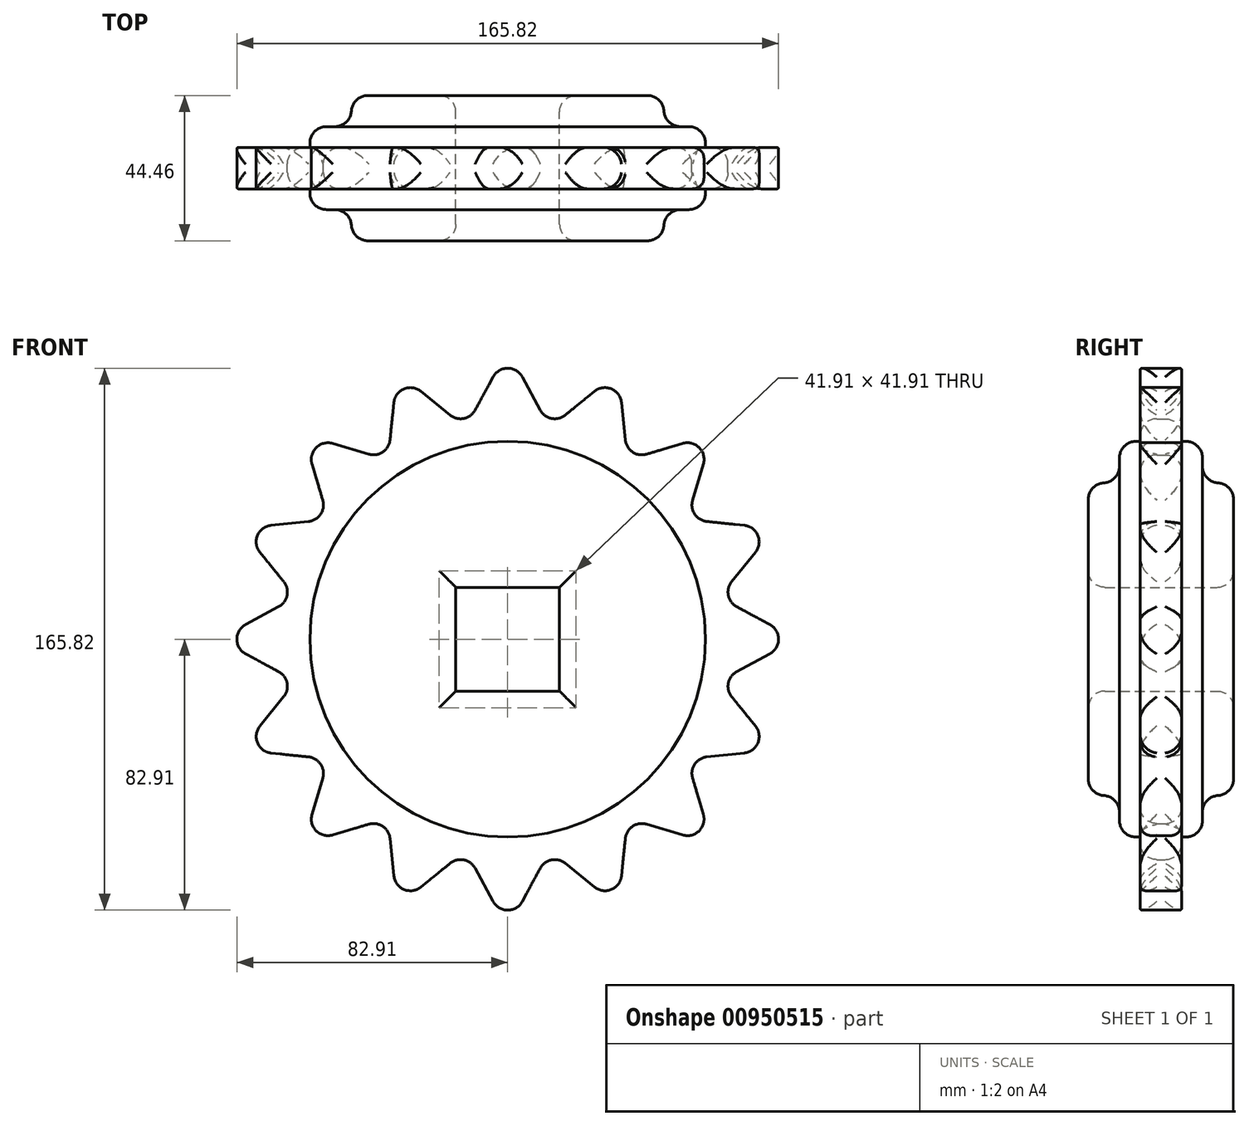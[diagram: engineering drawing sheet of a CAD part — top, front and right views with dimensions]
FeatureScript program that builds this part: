
annotation { "Feature Type Name" : "Feature", "Feature Type Description" : "" }
export const myFeature = defineFeature(function(context is Context, id is Id, definition is map)
    precondition{}
    {
        {
            var Q0;
            Q0=qCreatedBy(makeId("Front.planeOp"),FACE);
            var sketch = newSketch(context, id + "F0", { "sketchPlane" : qUnion([Q0])});
            skCircle(sketch, "E0", {"center": v(0, 0) * mm, "radius": 47.85 * mm});
            skLineSegment(sketch, "E1.bottom", {"start": v(-15.87, 15.88) * mm, "end": v(15.88, 15.88) * mm});
            skLineSegment(sketch, "E1.top", {"start": v(-15.88, -15.88) * mm, "end": v(15.87, -15.88) * mm});
            skLineSegment(sketch, "E1.left", {"start": v(-15.87, 15.88) * mm, "end": v(-15.88, -15.88) * mm});
            skLineSegment(sketch, "E1.right", {"start": v(15.88, 15.88) * mm, "end": v(15.87, -15.88) * mm});
            skCircle(sketch, "E2", {"center": v(0, 0) * mm, "radius": 60.55 * mm});
            skLineSegment(sketch, "E3", {"start": v(-16.33, 58.3) * mm, "end": v(0, 88.51) * mm});
            skLineSegment(sketch, "E4", {"start": v(16.33, 58.3) * mm, "end": v(0, 88.51) * mm});
            skLineSegment(sketch, "E5.1.0", {"start": v(-7.23, 60.12) * mm, "end": v(-33.87, 81.77) * mm});
            skLineSegment(sketch, "E5.2.0", {"start": v(-29.68, 52.78) * mm, "end": v(-62.59, 62.59) * mm});
            skLineSegment(sketch, "E5.3.0", {"start": v(-47.62, 37.4) * mm, "end": v(-81.77, 33.87) * mm});
            skLineSegment(sketch, "E5.4.0", {"start": v(-58.3, 16.33) * mm, "end": v(-88.51, 0) * mm});
            skLineSegment(sketch, "E5.5.0", {"start": v(-60.12, -7.23) * mm, "end": v(-81.77, -33.87) * mm});
            skLineSegment(sketch, "E5.6.0", {"start": v(-52.78, -29.68) * mm, "end": v(-62.59, -62.59) * mm});
            skLineSegment(sketch, "E5.7.0", {"start": v(-37.4, -47.62) * mm, "end": v(-33.87, -81.77) * mm});
            skLineSegment(sketch, "E5.8.0", {"start": v(-16.33, -58.3) * mm, "end": v(0, -88.51) * mm});
            skLineSegment(sketch, "E5.9.0", {"start": v(7.23, -60.12) * mm, "end": v(33.87, -81.77) * mm});
            skLineSegment(sketch, "E5.10.0", {"start": v(29.68, -52.78) * mm, "end": v(62.59, -62.59) * mm});
            skLineSegment(sketch, "E5.11.0", {"start": v(47.62, -37.4) * mm, "end": v(81.77, -33.87) * mm});
            skLineSegment(sketch, "E5.12.0", {"start": v(58.3, -16.33) * mm, "end": v(88.51, 0) * mm});
            skLineSegment(sketch, "E5.13.0", {"start": v(60.12, 7.23) * mm, "end": v(81.77, 33.87) * mm});
            skLineSegment(sketch, "E5.14.0", {"start": v(52.78, 29.68) * mm, "end": v(62.59, 62.59) * mm});
            skLineSegment(sketch, "E5.15.0", {"start": v(37.4, 47.62) * mm, "end": v(33.87, 81.77) * mm});
            skLineSegment(sketch, "E6.1.0", {"start": v(-37.4, 47.62) * mm, "end": v(-33.87, 81.77) * mm});
            skLineSegment(sketch, "E6.2.0", {"start": v(-52.78, 29.68) * mm, "end": v(-62.59, 62.59) * mm});
            skLineSegment(sketch, "E6.3.0", {"start": v(-60.12, 7.23) * mm, "end": v(-81.77, 33.87) * mm});
            skLineSegment(sketch, "E6.4.0", {"start": v(-58.3, -16.33) * mm, "end": v(-88.51, 0) * mm});
            skLineSegment(sketch, "E6.5.0", {"start": v(-47.62, -37.4) * mm, "end": v(-81.77, -33.87) * mm});
            skLineSegment(sketch, "E6.6.0", {"start": v(-29.68, -52.78) * mm, "end": v(-62.59, -62.59) * mm});
            skLineSegment(sketch, "E6.7.0", {"start": v(-7.23, -60.12) * mm, "end": v(-33.87, -81.77) * mm});
            skLineSegment(sketch, "E6.8.0", {"start": v(16.33, -58.3) * mm, "end": v(0, -88.51) * mm});
            skLineSegment(sketch, "E6.9.0", {"start": v(37.4, -47.62) * mm, "end": v(33.87, -81.77) * mm});
            skLineSegment(sketch, "E6.10.0", {"start": v(52.78, -29.68) * mm, "end": v(62.59, -62.59) * mm});
            skLineSegment(sketch, "E6.11.0", {"start": v(60.12, -7.23) * mm, "end": v(81.77, -33.87) * mm});
            skLineSegment(sketch, "E6.12.0", {"start": v(58.3, 16.33) * mm, "end": v(88.51, 0) * mm});
            skLineSegment(sketch, "E6.13.0", {"start": v(47.62, 37.4) * mm, "end": v(81.77, 33.87) * mm});
            skLineSegment(sketch, "E6.14.0", {"start": v(29.68, 52.78) * mm, "end": v(62.59, 62.59) * mm});
            skLineSegment(sketch, "E6.15.0", {"start": v(7.23, 60.12) * mm, "end": v(33.87, 81.77) * mm});
            skSolve(sketch);
        }
        {
            var Q0;
            {var subQ1=sQuery(id+"F0.wireOp",EDGE,"E2");var subQ7=sQuery(id+"F0.wireOp",EDGE,"E3");var subQ9=makeQuery(id+"F0.imprint","INTERSECT",VERTEX,{"derivedFrom":[subQ1,subQ7]});Q0=makeQuery(id+"F0.imprint","IMPRINT",FACE,{"disambiguationData":[TD([[makeQuery(id+"F0.imprint","IMPRINT",EDGE,{"disambiguationData":[TD([[subQ9,-1.0]])],"derivedFrom":subQ1}),-1.0]])]});}
            var Q1;
            {var subQ0=sQuery(id+"F0.wireOp",EDGE,"E5.3.0");var subQ1=sQuery(id+"F0.wireOp",EDGE,"E2");var subQ2=makeQuery(id+"F0.imprint","INTERSECT",VERTEX,{"derivedFrom":[subQ1,subQ0]});Q1=makeQuery(id+"F0.imprint","IMPRINT",FACE,{"disambiguationData":[TD([[makeQuery(id+"F0.imprint","IMPRINT",EDGE,{"disambiguationData":[TD([[subQ2,1.0]])],"derivedFrom":subQ1}),-1.0]])]});}
            var Q2;
            {var subQ0=sQuery(id+"F0.wireOp",EDGE,"E5.2.0");var subQ1=sQuery(id+"F0.wireOp",EDGE,"E2");var subQ2=makeQuery(id+"F0.imprint","INTERSECT",VERTEX,{"derivedFrom":[subQ1,subQ0]});Q2=makeQuery(id+"F0.imprint","IMPRINT",FACE,{"disambiguationData":[TD([[makeQuery(id+"F0.imprint","IMPRINT",EDGE,{"disambiguationData":[TD([[subQ2,-1.0]])],"derivedFrom":subQ1}),-1.0]])]});}
            var Q3;
            {var subQ0=sQuery(id+"F0.wireOp",EDGE,"E5.4.0");var subQ1=sQuery(id+"F0.wireOp",EDGE,"E2");var subQ2=makeQuery(id+"F0.imprint","INTERSECT",VERTEX,{"derivedFrom":[subQ1,subQ0]});Q3=makeQuery(id+"F0.imprint","IMPRINT",FACE,{"disambiguationData":[TD([[makeQuery(id+"F0.imprint","IMPRINT",EDGE,{"disambiguationData":[TD([[subQ2,1.0]])],"derivedFrom":subQ1}),-1.0]])]});}
            var Q4;
            {var subQ0=sQuery(id+"F0.wireOp",EDGE,"E5.5.0");var subQ1=sQuery(id+"F0.wireOp",EDGE,"E2");var subQ2=makeQuery(id+"F0.imprint","INTERSECT",VERTEX,{"derivedFrom":[subQ1,subQ0]});Q4=makeQuery(id+"F0.imprint","IMPRINT",FACE,{"disambiguationData":[TD([[makeQuery(id+"F0.imprint","IMPRINT",EDGE,{"disambiguationData":[TD([[subQ2,1.0]])],"derivedFrom":subQ1}),-1.0]])]});}
            var Q5;
            {var subQ0=sQuery(id+"F0.wireOp",EDGE,"E5.6.0");var subQ1=sQuery(id+"F0.wireOp",EDGE,"E2");var subQ2=makeQuery(id+"F0.imprint","INTERSECT",VERTEX,{"derivedFrom":[subQ1,subQ0]});Q5=makeQuery(id+"F0.imprint","IMPRINT",FACE,{"disambiguationData":[TD([[makeQuery(id+"F0.imprint","IMPRINT",EDGE,{"disambiguationData":[TD([[subQ2,1.0]])],"derivedFrom":subQ1}),-1.0]])]});}
            var Q6;
            {var subQ0=sQuery(id+"F0.wireOp",EDGE,"E5.7.0");var subQ1=sQuery(id+"F0.wireOp",EDGE,"E2");var subQ2=makeQuery(id+"F0.imprint","INTERSECT",VERTEX,{"derivedFrom":[subQ1,subQ0]});Q6=makeQuery(id+"F0.imprint","IMPRINT",FACE,{"disambiguationData":[TD([[makeQuery(id+"F0.imprint","IMPRINT",EDGE,{"disambiguationData":[TD([[subQ2,1.0]])],"derivedFrom":subQ1}),-1.0]])]});}
            var Q7;
            {var subQ0=sQuery(id+"F0.wireOp",EDGE,"E5.8.0");var subQ1=sQuery(id+"F0.wireOp",EDGE,"E2");var subQ2=makeQuery(id+"F0.imprint","INTERSECT",VERTEX,{"derivedFrom":[subQ1,subQ0]});Q7=makeQuery(id+"F0.imprint","IMPRINT",FACE,{"disambiguationData":[TD([[makeQuery(id+"F0.imprint","IMPRINT",EDGE,{"disambiguationData":[TD([[subQ2,1.0]])],"derivedFrom":subQ1}),-1.0]])]});}
            var Q8;
            {var subQ0=sQuery(id+"F0.wireOp",EDGE,"E5.9.0");var subQ1=sQuery(id+"F0.wireOp",EDGE,"E2");var subQ2=makeQuery(id+"F0.imprint","INTERSECT",VERTEX,{"derivedFrom":[subQ1,subQ0]});Q8=makeQuery(id+"F0.imprint","IMPRINT",FACE,{"disambiguationData":[TD([[makeQuery(id+"F0.imprint","IMPRINT",EDGE,{"disambiguationData":[TD([[subQ2,1.0]])],"derivedFrom":subQ1}),-1.0]])]});}
            var Q9;
            {var subQ0=sQuery(id+"F0.wireOp",EDGE,"E5.10.0");var subQ1=sQuery(id+"F0.wireOp",EDGE,"E2");var subQ2=makeQuery(id+"F0.imprint","INTERSECT",VERTEX,{"derivedFrom":[subQ1,subQ0]});Q9=makeQuery(id+"F0.imprint","IMPRINT",FACE,{"disambiguationData":[TD([[makeQuery(id+"F0.imprint","IMPRINT",EDGE,{"disambiguationData":[TD([[subQ2,1.0]])],"derivedFrom":subQ1}),-1.0]])]});}
            var Q10;
            {var subQ0=sQuery(id+"F0.wireOp",EDGE,"E5.11.0");var subQ1=sQuery(id+"F0.wireOp",EDGE,"E2");var subQ2=makeQuery(id+"F0.imprint","INTERSECT",VERTEX,{"derivedFrom":[subQ1,subQ0]});Q10=makeQuery(id+"F0.imprint","IMPRINT",FACE,{"disambiguationData":[TD([[makeQuery(id+"F0.imprint","IMPRINT",EDGE,{"disambiguationData":[TD([[subQ2,1.0]])],"derivedFrom":subQ1}),-1.0]])]});}
            var Q11;
            {var subQ0=sQuery(id+"F0.wireOp",EDGE,"E5.12.0");var subQ1=sQuery(id+"F0.wireOp",EDGE,"E2");var subQ2=makeQuery(id+"F0.imprint","INTERSECT",VERTEX,{"derivedFrom":[subQ1,subQ0]});Q11=makeQuery(id+"F0.imprint","IMPRINT",FACE,{"disambiguationData":[TD([[makeQuery(id+"F0.imprint","IMPRINT",EDGE,{"disambiguationData":[TD([[subQ2,1.0]])],"derivedFrom":subQ1}),-1.0]])]});}
            var Q12;
            {var subQ0=sQuery(id+"F0.wireOp",EDGE,"E5.13.0");var subQ1=sQuery(id+"F0.wireOp",EDGE,"E2");var subQ2=makeQuery(id+"F0.imprint","INTERSECT",VERTEX,{"derivedFrom":[subQ1,subQ0]});Q12=makeQuery(id+"F0.imprint","IMPRINT",FACE,{"disambiguationData":[TD([[makeQuery(id+"F0.imprint","IMPRINT",EDGE,{"disambiguationData":[TD([[subQ2,1.0]])],"derivedFrom":subQ1}),-1.0]])]});}
            var Q13;
            {var subQ1=sQuery(id+"F0.wireOp",EDGE,"E2");var subQ5=sQuery(id+"F0.wireOp",EDGE,"E5.14.0");var subQ6=makeQuery(id+"F0.imprint","INTERSECT",VERTEX,{"derivedFrom":[subQ1,subQ5]});Q13=makeQuery(id+"F0.imprint","IMPRINT",FACE,{"disambiguationData":[TD([[makeQuery(id+"F0.imprint","IMPRINT",EDGE,{"disambiguationData":[TD([[subQ6,1.0]])],"derivedFrom":subQ1}),-1.0]])]});}
            var Q14;
            {var subQ1=sQuery(id+"F0.wireOp",EDGE,"E2");var subQ5=sQuery(id+"F0.wireOp",EDGE,"E5.15.0");var subQ6=makeQuery(id+"F0.imprint","INTERSECT",VERTEX,{"derivedFrom":[subQ1,subQ5]});Q14=makeQuery(id+"F0.imprint","IMPRINT",FACE,{"disambiguationData":[TD([[makeQuery(id+"F0.imprint","IMPRINT",EDGE,{"disambiguationData":[TD([[subQ6,1.0]])],"derivedFrom":subQ1}),-1.0]])]});}
            var Q15;
            {var subQ1=sQuery(id+"F0.wireOp",EDGE,"E2");var subQ5=sQuery(id+"F0.wireOp",EDGE,"E4");var subQ6=makeQuery(id+"F0.imprint","INTERSECT",VERTEX,{"derivedFrom":[subQ1,subQ5]});Q15=makeQuery(id+"F0.imprint","IMPRINT",FACE,{"disambiguationData":[TD([[makeQuery(id+"F0.imprint","IMPRINT",EDGE,{"disambiguationData":[TD([[subQ6,1.0]])],"derivedFrom":subQ1}),-1.0]])]});}
            var Q16;
            {var subQ0=sQuery(id+"F0.wireOp",EDGE,"E5.1.0");var subQ1=sQuery(id+"F0.wireOp",EDGE,"E2");var subQ2=makeQuery(id+"F0.imprint","INTERSECT",VERTEX,{"derivedFrom":[subQ1,subQ0]});Q16=makeQuery(id+"F0.imprint","IMPRINT",FACE,{"disambiguationData":[TD([[makeQuery(id+"F0.imprint","IMPRINT",EDGE,{"disambiguationData":[TD([[subQ2,1.0]])],"derivedFrom":subQ1}),-1.0]])]});}
            var Q17;
            {var subQ0=sQuery(id+"F0.wireOp",EDGE,"E3");var subQ1=sQuery(id+"F0.wireOp",EDGE,"E2");var subQ2=makeQuery(id+"F0.imprint","INTERSECT",VERTEX,{"derivedFrom":[subQ1,subQ0]});Q17=makeQuery(id+"F0.imprint","IMPRINT",FACE,{"disambiguationData":[TD([[makeQuery(id+"F0.imprint","IMPRINT",EDGE,{"disambiguationData":[TD([[subQ2,1.0]])],"derivedFrom":subQ1}),-1.0]])]});}
            var Q18;
            {var subQ0=sQuery(id+"F0.wireOp",EDGE,"E4");var subQ1=sQuery(id+"F0.wireOp",EDGE,"E2");var subQ2=makeQuery(id+"F0.imprint","INTERSECT",VERTEX,{"derivedFrom":[subQ1,subQ0]});Q18=makeQuery(id+"F0.imprint","IMPRINT",FACE,{"disambiguationData":[TD([[makeQuery(id+"F0.imprint","IMPRINT",EDGE,{"disambiguationData":[TD([[subQ2,-1.0]])],"derivedFrom":subQ1}),-1.0]])]});}
            var Q19;
            {var subQ0=sQuery(id+"F0.wireOp",EDGE,"E5.15.0");var subQ1=sQuery(id+"F0.wireOp",EDGE,"E2");var subQ2=makeQuery(id+"F0.imprint","INTERSECT",VERTEX,{"derivedFrom":[subQ1,subQ0]});Q19=makeQuery(id+"F0.imprint","IMPRINT",FACE,{"disambiguationData":[TD([[makeQuery(id+"F0.imprint","IMPRINT",EDGE,{"disambiguationData":[TD([[subQ2,-1.0]])],"derivedFrom":subQ1}),-1.0]])]});}
            var Q20;
            {var subQ0=sQuery(id+"F0.wireOp",EDGE,"E5.14.0");var subQ1=sQuery(id+"F0.wireOp",EDGE,"E2");var subQ2=makeQuery(id+"F0.imprint","INTERSECT",VERTEX,{"derivedFrom":[subQ1,subQ0]});Q20=makeQuery(id+"F0.imprint","IMPRINT",FACE,{"disambiguationData":[TD([[makeQuery(id+"F0.imprint","IMPRINT",EDGE,{"disambiguationData":[TD([[subQ2,-1.0]])],"derivedFrom":subQ1}),-1.0]])]});}
            var Q21;
            {var subQ0=sQuery(id+"F0.wireOp",EDGE,"E5.13.0");var subQ1=sQuery(id+"F0.wireOp",EDGE,"E2");var subQ2=makeQuery(id+"F0.imprint","INTERSECT",VERTEX,{"derivedFrom":[subQ1,subQ0]});Q21=makeQuery(id+"F0.imprint","IMPRINT",FACE,{"disambiguationData":[TD([[makeQuery(id+"F0.imprint","IMPRINT",EDGE,{"disambiguationData":[TD([[subQ2,-1.0]])],"derivedFrom":subQ1}),-1.0]])]});}
            var Q22;
            {var subQ0=sQuery(id+"F0.wireOp",EDGE,"E5.3.0");var subQ1=sQuery(id+"F0.wireOp",EDGE,"E2");var subQ2=makeQuery(id+"F0.imprint","INTERSECT",VERTEX,{"derivedFrom":[subQ1,subQ0]});Q22=makeQuery(id+"F0.imprint","IMPRINT",FACE,{"disambiguationData":[TD([[makeQuery(id+"F0.imprint","IMPRINT",EDGE,{"disambiguationData":[TD([[subQ2,-1.0]])],"derivedFrom":subQ1}),-1.0]])]});}
            var Q23;
            {var subQ0=sQuery(id+"F0.wireOp",EDGE,"E5.4.0");var subQ1=sQuery(id+"F0.wireOp",EDGE,"E2");var subQ2=makeQuery(id+"F0.imprint","INTERSECT",VERTEX,{"derivedFrom":[subQ1,subQ0]});Q23=makeQuery(id+"F0.imprint","IMPRINT",FACE,{"disambiguationData":[TD([[makeQuery(id+"F0.imprint","IMPRINT",EDGE,{"disambiguationData":[TD([[subQ2,-1.0]])],"derivedFrom":subQ1}),-1.0]])]});}
            var Q24;
            {var subQ0=sQuery(id+"F0.wireOp",EDGE,"E5.5.0");var subQ1=sQuery(id+"F0.wireOp",EDGE,"E2");var subQ2=makeQuery(id+"F0.imprint","INTERSECT",VERTEX,{"derivedFrom":[subQ1,subQ0]});Q24=makeQuery(id+"F0.imprint","IMPRINT",FACE,{"disambiguationData":[TD([[makeQuery(id+"F0.imprint","IMPRINT",EDGE,{"disambiguationData":[TD([[subQ2,-1.0]])],"derivedFrom":subQ1}),-1.0]])]});}
            var Q25;
            {var subQ0=sQuery(id+"F0.wireOp",EDGE,"E5.6.0");var subQ1=sQuery(id+"F0.wireOp",EDGE,"E2");var subQ2=makeQuery(id+"F0.imprint","INTERSECT",VERTEX,{"derivedFrom":[subQ1,subQ0]});Q25=makeQuery(id+"F0.imprint","IMPRINT",FACE,{"disambiguationData":[TD([[makeQuery(id+"F0.imprint","IMPRINT",EDGE,{"disambiguationData":[TD([[subQ2,-1.0]])],"derivedFrom":subQ1}),-1.0]])]});}
            var Q26;
            {var subQ0=sQuery(id+"F0.wireOp",EDGE,"E5.7.0");var subQ1=sQuery(id+"F0.wireOp",EDGE,"E2");var subQ2=makeQuery(id+"F0.imprint","INTERSECT",VERTEX,{"derivedFrom":[subQ1,subQ0]});Q26=makeQuery(id+"F0.imprint","IMPRINT",FACE,{"disambiguationData":[TD([[makeQuery(id+"F0.imprint","IMPRINT",EDGE,{"disambiguationData":[TD([[subQ2,-1.0]])],"derivedFrom":subQ1}),-1.0]])]});}
            var Q27;
            {var subQ0=sQuery(id+"F0.wireOp",EDGE,"E5.8.0");var subQ1=sQuery(id+"F0.wireOp",EDGE,"E2");var subQ2=makeQuery(id+"F0.imprint","INTERSECT",VERTEX,{"derivedFrom":[subQ1,subQ0]});Q27=makeQuery(id+"F0.imprint","IMPRINT",FACE,{"disambiguationData":[TD([[makeQuery(id+"F0.imprint","IMPRINT",EDGE,{"disambiguationData":[TD([[subQ2,-1.0]])],"derivedFrom":subQ1}),-1.0]])]});}
            var Q28;
            {var subQ0=sQuery(id+"F0.wireOp",EDGE,"E5.9.0");var subQ1=sQuery(id+"F0.wireOp",EDGE,"E2");var subQ2=makeQuery(id+"F0.imprint","INTERSECT",VERTEX,{"derivedFrom":[subQ1,subQ0]});Q28=makeQuery(id+"F0.imprint","IMPRINT",FACE,{"disambiguationData":[TD([[makeQuery(id+"F0.imprint","IMPRINT",EDGE,{"disambiguationData":[TD([[subQ2,-1.0]])],"derivedFrom":subQ1}),-1.0]])]});}
            var Q29;
            {var subQ0=sQuery(id+"F0.wireOp",EDGE,"E5.10.0");var subQ1=sQuery(id+"F0.wireOp",EDGE,"E2");var subQ2=makeQuery(id+"F0.imprint","INTERSECT",VERTEX,{"derivedFrom":[subQ1,subQ0]});Q29=makeQuery(id+"F0.imprint","IMPRINT",FACE,{"disambiguationData":[TD([[makeQuery(id+"F0.imprint","IMPRINT",EDGE,{"disambiguationData":[TD([[subQ2,-1.0]])],"derivedFrom":subQ1}),-1.0]])]});}
            var Q30;
            {var subQ0=sQuery(id+"F0.wireOp",EDGE,"E5.11.0");var subQ1=sQuery(id+"F0.wireOp",EDGE,"E2");var subQ2=makeQuery(id+"F0.imprint","INTERSECT",VERTEX,{"derivedFrom":[subQ1,subQ0]});Q30=makeQuery(id+"F0.imprint","IMPRINT",FACE,{"disambiguationData":[TD([[makeQuery(id+"F0.imprint","IMPRINT",EDGE,{"disambiguationData":[TD([[subQ2,-1.0]])],"derivedFrom":subQ1}),-1.0]])]});}
            var Q31;
            {var subQ0=sQuery(id+"F0.wireOp",EDGE,"E5.12.0");var subQ1=sQuery(id+"F0.wireOp",EDGE,"E2");var subQ2=makeQuery(id+"F0.imprint","INTERSECT",VERTEX,{"derivedFrom":[subQ1,subQ0]});Q31=makeQuery(id+"F0.imprint","IMPRINT",FACE,{"disambiguationData":[TD([[makeQuery(id+"F0.imprint","IMPRINT",EDGE,{"disambiguationData":[TD([[subQ2,-1.0]])],"derivedFrom":subQ1}),-1.0]])]});}
            extrude(context, id + "F1", {"entities" : qUnion([Q0, Q1, Q2, Q3, Q4, Q5, Q6, Q7, Q8, Q9, Q10, Q11, Q12, Q13, Q14, Q15, Q16, Q17, Q18, Q19, Q20, Q21, Q22, Q23, Q24, Q25, Q26, Q27, Q28, Q29, Q30, Q31]), "endBound" : BoundingType.SYMMETRIC, "depth" : 12.7 * mm, "offsetDistance" : 25.4 * mm});
        }
        {
            var Q0;
            Q0=makeQuery(id+"F0.imprint","IMPRINT",FACE,{"disambiguationData":[TD([[makeQuery(id+"F0.imprint","IMPRINT",EDGE,{"derivedFrom":sQuery(id+"F0.wireOp",EDGE,"E0")}),-1.0]])]});
            extrude(context, id + "F2", {"entities" : qUnion([Q0]), "operationType" : NewBodyOperationType.ADD, "endBound" : BoundingType.SYMMETRIC, "depth" : 25.4 * mm, "offsetDistance" : 25.4 * mm});
        }
        {
            var Q0;
            Q0=makeQuery(id+"F0.imprint","IMPRINT",FACE,{"disambiguationData":[TD([[makeQuery(id+"F0.imprint","IMPRINT",EDGE,{"derivedFrom":sQuery(id+"F0.wireOp",EDGE,"E0")}),1.0]])]});
            extrude(context, id + "F3", {"entities" : qUnion([Q0]), "operationType" : NewBodyOperationType.ADD, "endBound" : BoundingType.SYMMETRIC, "depth" : 44.45 * mm, "offsetDistance" : 25.4 * mm});
        }
        {
            var Q0;
            Q0=makeQuery(id+"F1.opExtrude","SWEPT_FACE",FACE,{"disambiguationData":[OSD([sQuery(id+"F0.wireOp",EDGE,"E5.3.0")])]});
            var Q1;
            Q1=makeQuery(id+"F1.opExtrude","SWEPT_FACE",FACE,{"disambiguationData":[OSD([sQuery(id+"F0.wireOp",EDGE,"E5.2.0")])]});
            var Q2;
            Q2=makeQuery(id+"F1.opExtrude","SWEPT_FACE",FACE,{"disambiguationData":[OSD([sQuery(id+"F0.wireOp",EDGE,"E5.1.0")])]});
            var Q3;
            Q3=makeQuery(id+"F1.opExtrude","SWEPT_FACE",FACE,{"disambiguationData":[OSD([sQuery(id+"F0.wireOp",EDGE,"E4")])]});
            var Q4;
            Q4=makeQuery(id+"F1.opExtrude","SWEPT_FACE",FACE,{"disambiguationData":[OSD([sQuery(id+"F0.wireOp",EDGE,"E5.15.0")])]});
            var Q5;
            Q5=makeQuery(id+"F1.opExtrude","SWEPT_FACE",FACE,{"disambiguationData":[OSD([sQuery(id+"F0.wireOp",EDGE,"E5.14.0")])]});
            var Q6;
            Q6=makeQuery(id+"F1.opExtrude","SWEPT_FACE",FACE,{"disambiguationData":[OSD([sQuery(id+"F0.wireOp",EDGE,"E5.13.0")])]});
            var Q7;
            Q7=makeQuery(id+"F1.opExtrude","SWEPT_FACE",FACE,{"disambiguationData":[OSD([sQuery(id+"F0.wireOp",EDGE,"E5.12.0")])]});
            var Q8;
            Q8=makeQuery(id+"F1.opExtrude","SWEPT_FACE",FACE,{"disambiguationData":[OSD([sQuery(id+"F0.wireOp",EDGE,"E5.11.0")])]});
            var Q9;
            Q9=makeQuery(id+"F1.opExtrude","SWEPT_FACE",FACE,{"disambiguationData":[OSD([sQuery(id+"F0.wireOp",EDGE,"E5.10.0")])]});
            var Q10;
            Q10=makeQuery(id+"F1.opExtrude","SWEPT_FACE",FACE,{"disambiguationData":[OSD([sQuery(id+"F0.wireOp",EDGE,"E5.9.0")])]});
            var Q11;
            Q11=makeQuery(id+"F1.opExtrude","SWEPT_FACE",FACE,{"disambiguationData":[OSD([sQuery(id+"F0.wireOp",EDGE,"E5.8.0")])]});
            var Q12;
            Q12=makeQuery(id+"F1.opExtrude","SWEPT_FACE",FACE,{"disambiguationData":[OSD([sQuery(id+"F0.wireOp",EDGE,"E5.7.0")])]});
            var Q13;
            Q13=makeQuery(id+"F1.opExtrude","SWEPT_FACE",FACE,{"disambiguationData":[OSD([sQuery(id+"F0.wireOp",EDGE,"E5.6.0")])]});
            var Q14;
            Q14=makeQuery(id+"F1.opExtrude","SWEPT_FACE",FACE,{"disambiguationData":[OSD([sQuery(id+"F0.wireOp",EDGE,"E5.5.0")])]});
            var Q15;
            Q15=makeQuery(id+"F1.opExtrude","SWEPT_FACE",FACE,{"disambiguationData":[OSD([sQuery(id+"F0.wireOp",EDGE,"E5.4.0")])]});
            fillet(context, id + "F4", {"entities" : qUnion([Q0, Q1, Q2, Q3, Q4, Q5, Q6, Q7, Q8, Q9, Q10, Q11, Q12, Q13, Q14, Q15]), "radius" : 5.08 * mm, "tangentPropagation" : true, "allowEdgeOverflow" : false});
        }
        {
            var Q0;
            Q0=makeQuery(id+"F3.opExtrude","CAP_FACE",FACE,{"disambiguationData":[OSD([sQuery(id+"F0.wireOp",EDGE,"E0"),sQuery(id+"F0.wireOp",EDGE,"E1.bottom"),sQuery(id+"F0.wireOp",EDGE,"E1.top"),sQuery(id+"F0.wireOp",EDGE,"E1.left"),sQuery(id+"F0.wireOp",EDGE,"E1.right")])],"isStart":false});
            var Q1;
            Q1=makeQuery(id+"F3.opExtrude","CAP_FACE",FACE,{"disambiguationData":[OSD([sQuery(id+"F0.wireOp",EDGE,"E0"),sQuery(id+"F0.wireOp",EDGE,"E1.bottom"),sQuery(id+"F0.wireOp",EDGE,"E1.top"),sQuery(id+"F0.wireOp",EDGE,"E1.left"),sQuery(id+"F0.wireOp",EDGE,"E1.right")])],"isStart":true});
            fillet(context, id + "F5", {"entities" : qUnion([Q0, Q1]), "radius" : 5.08 * mm, "tangentPropagation" : true, "allowEdgeOverflow" : false});
        }
        {
            var Q0;
            Q0=makeQuery(id+"F2.opExtrude","CAP_FACE",FACE,{"disambiguationData":[OSD([sQuery(id+"F0.wireOp",EDGE,"E0"),sQuery(id+"F0.wireOp",EDGE,"E2")])],"isStart":false});
            var Q1;
            Q1=makeQuery(id+"F2.opExtrude","CAP_FACE",FACE,{"disambiguationData":[OSD([sQuery(id+"F0.wireOp",EDGE,"E0"),sQuery(id+"F0.wireOp",EDGE,"E2")])],"isStart":true});
            fillet(context, id + "F6", {"entities" : qUnion([Q0, Q1]), "radius" : 5.08 * mm, "tangentPropagation" : true, "allowEdgeOverflow" : false});
        }
    });
